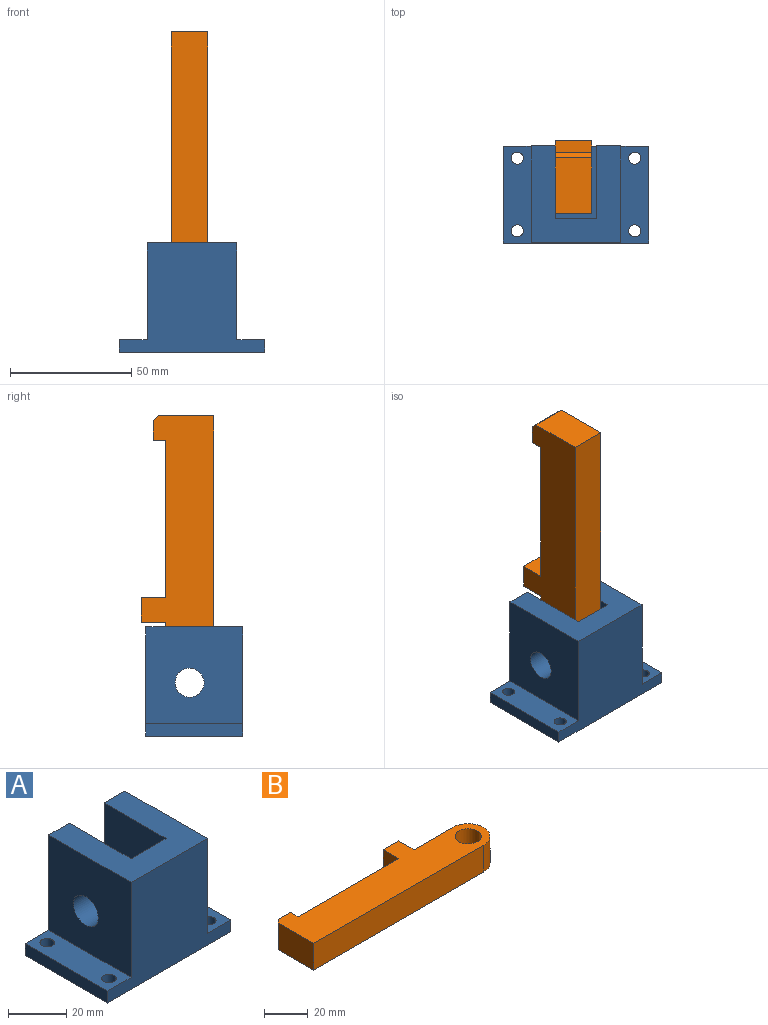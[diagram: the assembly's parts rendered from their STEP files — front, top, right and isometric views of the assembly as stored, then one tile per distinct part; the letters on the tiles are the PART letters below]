
ASSEMBLY  parts=2 mates=1
PART A: 20 faces, bbox 60x40x45 mm
  f0: plane 30x17mm, normal (0,0,1), area 510mm2, adj f4,f14,f15,f16
  f1: plane 40x11.5mm, normal (0,0,1), area 420.7mm2, adj f2,f3,f4,f5,f9,f13
  f2: plane 60x45mm, normal (0,-1,0), area 1780mm2, adj f1,f3,f8,f10,f11,f12,f13,f17
  f3: plane 40x5mm, normal (1,0,0), area 200mm2, adj f1,f2,f4,f10
  f4: plane 60x45mm, normal (0,1,0), area 1100mm2, adj f0,f1,f3,f8,f10,f11,f12,f13
  f5: cylinder r=2.5mm len=5mm, axis (0,0,1), area 78.5mm2, adj f1,f10
  f6: cylinder r=2.5mm len=5mm, axis (0,0,1), area 78.5mm2, adj f10,f11
  f7: cylinder r=2.5mm len=5mm, axis (0,0,1), area 78.5mm2, adj f10,f11
  f8: plane 40x5mm, normal (-1,0,0), area 200mm2, adj f2,f4,f10,f11
  f9: cylinder r=2.5mm len=5mm, axis (0,0,1), area 78.5mm2, adj f1,f10
  f10: plane 60x40mm, normal (0,0,-1), area 2321.5mm2, adj f2,f3,f4,f5,f6,f7,f8,f9
  f11: plane 40x11.5mm, normal (0,0,1), area 420.7mm2, adj f2,f4,f6,f7,f8,f12
  f12: plane 40x40mm, normal (-1,0,0), area 1486.9mm2, adj f2,f4,f11,f17,f18
  f13: plane 40x40mm, normal (1,0,0), area 1486.9mm2, adj f1,f2,f4,f17,f19
  f14: plane 40x30mm, normal (-1,0,0), area 1086.9mm2, adj f0,f4,f15,f17,f19
  f15: plane 40x17mm, normal (0,1,0), area 680mm2, adj f0,f14,f16,f17
  f16: plane 40x30mm, normal (1,0,0), area 1086.9mm2, adj f0,f4,f15,f17,f18
  f17: plane 40x37mm, normal (0,0,1), area 970mm2, adj f2,f4,f12,f13,f14,f15,f16
  f18: cylinder r=6mm len=12mm, axis (1,0,0), area 377mm2, adj f12,f16
  f19: cylinder r=6mm len=12mm, axis (1,0,0), area 377mm2, adj f13,f14
PART B: 14 faces, bbox 120x30x15 mm
  f0: plane 22.88x15mm, normal (-1,0,0), area 343.1mm2, adj f1,f10,f11,f12
  f1: plane 110x15mm, normal (0,-1,0), area 1650mm2, adj f0,f11,f12,f13
  f2: plane 25x15mm, normal (0,1,0), area 375mm2, adj f3,f11,f12,f13
  f3: plane 15x10mm, normal (1,0,0), area 150mm2, adj f2,f4,f11,f12
  f4: plane 15x10mm, normal (0,1,0), area 150mm2, adj f3,f5,f11,f12
  f5: plane 15x10mm, normal (-1,0,0), area 150mm2, adj f4,f6,f11,f12
  f6: plane 65x15mm, normal (0,1,0), area 975mm2, adj f5,f7,f11,f12
  f7: plane 15x5mm, normal (1,0,0), area 75mm2, adj f6,f8,f11,f12
  f8: plane 15x8.02mm, normal (0,1,0), area 120.3mm2, adj f7,f10,f11,f12
  f9: cylinder r=6mm len=15mm, axis (0,0,-1), area 565.5mm2, adj f11,f12
  f10: plane 15x2.13mm, normal (-0.73,0.68,0), area 43.5mm2, adj f0,f8,f11,f12
  f11: plane 120x30mm, normal (0,0,1), area 2391.9mm2, adj f0,f1,f2,f3,f4,f5,f6,f7
  f12: plane 120x30mm, normal (0,0,-1), area 2391.9mm2, adj f0,f1,f2,f3,f4,f5,f6,f7
  f13: cylinder r=10mm len=20mm, axis (0,0,-1), area 471.2mm2, adj f1,f2,f11,f12
PLACE A t=(0,48.74,-56.82)mm
PLACE B rot(axis=(0,1,0),90deg) t=(-8.5,100.74,28.18)mm
MATE revolute B.f9 <-> A.f18  axis (-1,0,0) through (-8.5,90.74,-39.82)mm
